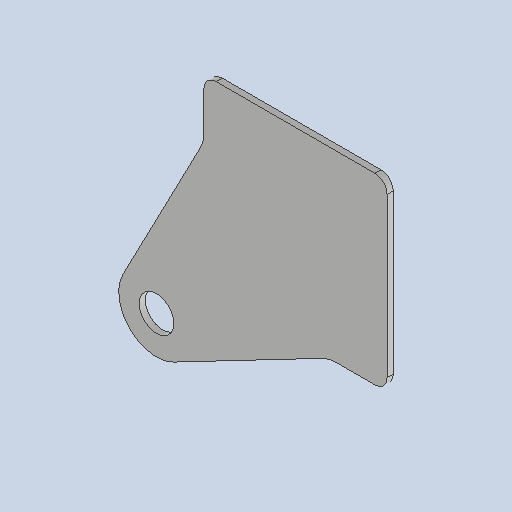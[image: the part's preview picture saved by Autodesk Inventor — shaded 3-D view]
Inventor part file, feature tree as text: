
AUTODESK INVENTOR PART (.ipt)
format: ipt  version: 2025 (Build 290162010, 162A)  size: 203,776 bytes
history: native  units: mm
features: other x2, sheet_metal_op x1, chamfer x1, sketch x1
ambient origin geometry x8: Origin, YZ Plane, XZ Plane, XY Plane, X Axis, Y Axis, Z Axis, Center Point
bodies: Solid1 (feature_tree)
feature tree (5):
  sheet_metal_op  "Face1"
  chamfer  "Corner Round3"
  sketch  "Sketch1"  dims[d2=80.0mm d3=80.0mm d6=3.0mm d29=5.0mm d30=17.0mm d31=10.0mm d32=40.0mm d34=5.0mm d35=15.0mm d36=25.0mm d37=6.0mm]
  other  "Plate1"
  other  "Definition1"
